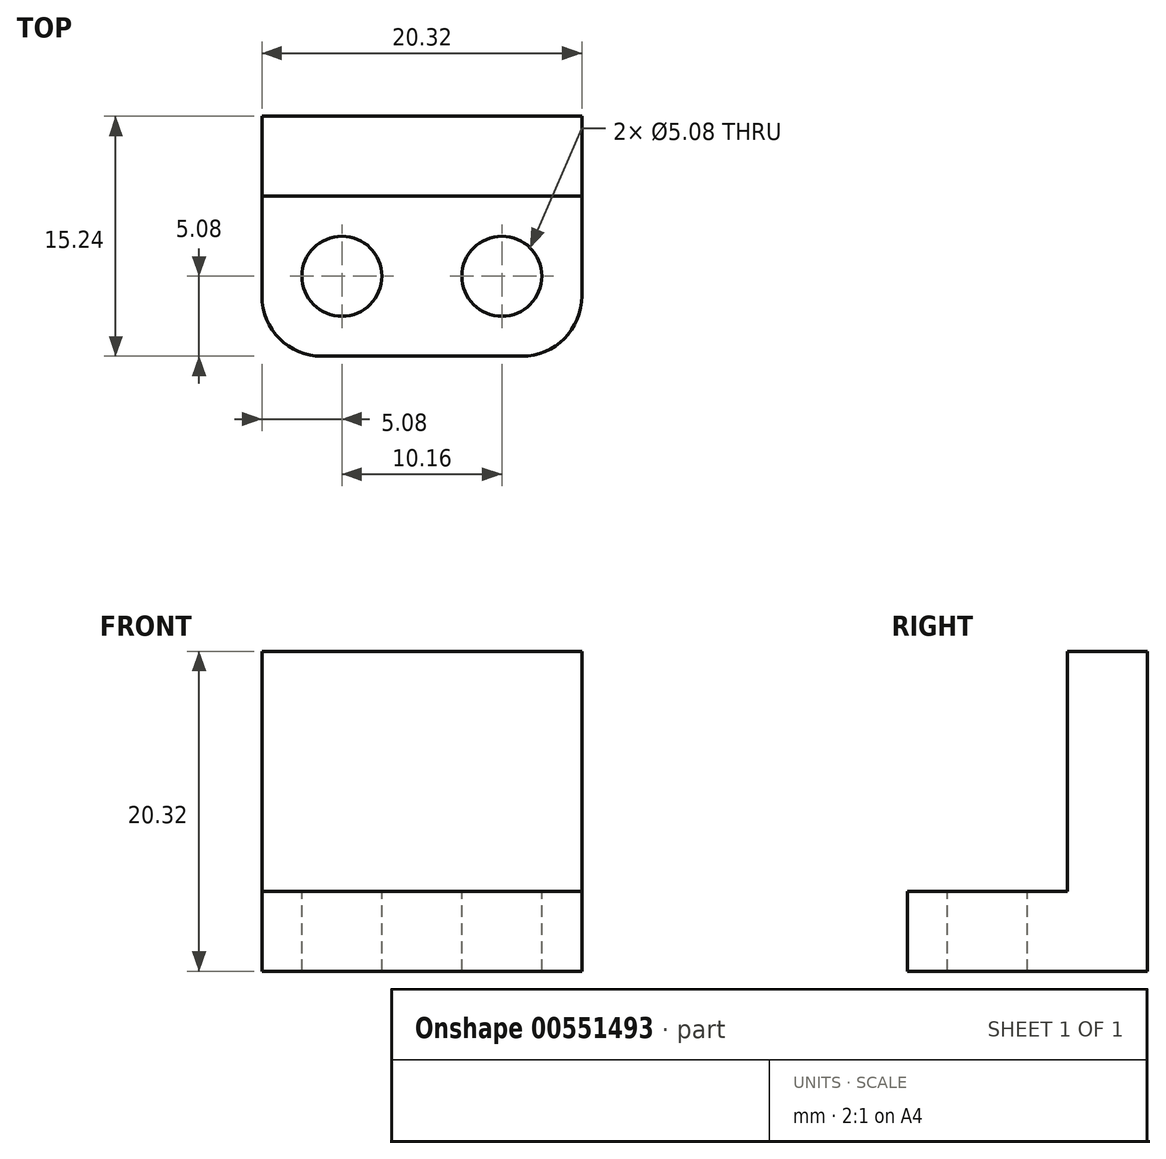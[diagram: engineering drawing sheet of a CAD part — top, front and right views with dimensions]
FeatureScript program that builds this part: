
annotation { "Feature Type Name" : "Feature", "Feature Type Description" : "" }
export const myFeature = defineFeature(function(context is Context, id is Id, definition is map)
    precondition{}
    {
        {
            var Q0;
            Q0=qCreatedBy(makeId("Front.planeOp"),FACE);
            var sketch = newSketch(context, id + "F0", { "sketchPlane" : qUnion([Q0])});
            skLineSegment(sketch, "E0", {"start": v(0, 0) * mm, "end": v(20.32, 0) * mm});
            skLineSegment(sketch, "E1", {"start": v(20.32, 0) * mm, "end": v(20.32, 5.08) * mm});
            skLineSegment(sketch, "E2", {"start": v(20.32, 5.08) * mm, "end": v(0, 5.08) * mm});
            skLineSegment(sketch, "E3", {"start": v(0, 5.08) * mm, "end": v(0, 0) * mm});
            skSolve(sketch);
        }
        {
            var Q0;
            Q0=makeQuery(id+"F0.imprint","IMPRINT",FACE,{"disambiguationData":[TD([[makeQuery(id+"F0.imprint","IMPRINT",EDGE,{"derivedFrom":sQuery(id+"F0.wireOp",EDGE,"E0")}),1.0]])]});
            extrude(context, id + "F1", {"entities" : qUnion([Q0]), "depth" : 15.24 * mm, "offsetDistance" : 25.4 * mm});
        }
        {
            var Q0;
            Q0=makeQuery(id+"F1.opExtrude","CAP_EDGE",EDGE,{"disambiguationData":[OSD([sQuery(id+"F0.wireOp",EDGE,"E1")])],"isStart":false});
            var Q1;
            Q1=makeQuery(id+"F1.opExtrude","CAP_EDGE",EDGE,{"disambiguationData":[OSD([sQuery(id+"F0.wireOp",EDGE,"E3")])],"isStart":false});
            fillet(context, id + "F2", {"entities" : qUnion([Q0, Q1]), "radius" : 3.8 * mm, "tangentPropagation" : true, "allowEdgeOverflow" : false});
        }
        {
            var Q0;
            Q0=makeQuery(id+"F1.opExtrude","SWEPT_FACE",FACE,{"disambiguationData":[OSD([sQuery(id+"F0.wireOp",EDGE,"E2")])]});
            var sketch = newSketch(context, id + "F3", { "sketchPlane" : qUnion([Q0])});
            skLineSegment(sketch, "E4", {"start": v(5.08, -10.16) * mm, "end": v(15.24, -10.16) * mm, "construction": true});
            skCircle(sketch, "E5", {"center": v(15.24, -10.16) * mm, "radius": 2.54 * mm});
            skCircle(sketch, "E6", {"center": v(5.08, -10.16) * mm, "radius": 2.54 * mm});
            skSolve(sketch);
        }
        {
            var Q0;
            Q0=sQuery(id+"F3.wireOp",VERTEX,"E4.start");
            var Q1;
            Q1=sQuery(id+"F3.wireOp",VERTEX,"E5.center");
            var Q2;
            Q2=makeQuery(id+"F1.opExtrude","SWEPT_BODY",BODY,{"disambiguationData":[OSD([sQuery(id+"F0.wireOp",EDGE,"E0"),sQuery(id+"F0.wireOp",EDGE,"E1"),sQuery(id+"F0.wireOp",EDGE,"E2"),sQuery(id+"F0.wireOp",EDGE,"E3")])]});
            hole(context, id + "F4", {"style" : HoleStyle.SIMPLE, "endStyle" : HoleEndStyle.THROUGH, "holeDiameter" : 5.08 * mm, "isTappedThrough" : true, "tappedDepth" : 12.7 * mm, "tapClearance" : 3, "locations" : qUnion([Q0, Q1]), "scope" : qUnion([Q2])});
        }
        {
            var Q0;
            Q0=makeQuery(id+"F1.opExtrude","SWEPT_FACE",FACE,{"disambiguationData":[OSD([sQuery(id+"F0.wireOp",EDGE,"E2")])]});
            var sketch = newSketch(context, id + "F5", { "sketchPlane" : qUnion([Q0])});
            skLineSegment(sketch, "E7", {"start": v(0, 0) * mm, "end": v(20.32, 0) * mm});
            skLineSegment(sketch, "E8", {"start": v(20.32, 0) * mm, "end": v(20.32, -5.08) * mm});
            skLineSegment(sketch, "E9", {"start": v(20.32, -5.08) * mm, "end": v(0, -5.08) * mm});
            skLineSegment(sketch, "E10", {"start": v(0, -5.08) * mm, "end": v(0, 0) * mm});
            skSolve(sketch);
        }
        {
            var Q0;
            Q0=makeQuery(id+"F5.imprint","IMPRINT",FACE,{"disambiguationData":[TD([[makeQuery(id+"F5.imprint","IMPRINT",EDGE,{"derivedFrom":sQuery(id+"F5.wireOp",EDGE,"E7")}),1.0]])]});
            extrude(context, id + "F6", {"entities" : qUnion([Q0]), "operationType" : NewBodyOperationType.ADD, "depth" : 15.24 * mm, "offsetDistance" : 25.4 * mm});
        }
    });
